# Revit family: UM375 Silla Lisa
name_source: partatom
category: Mobiliario
units: mm (PartAtom-declared; Revit-internal decimal feet)

## family parameters
Compartido = No
Corte con vacíos al cargar = No
Número OmniClass = 23.40.20.00
Punto de cálculo de habitación = No
Se basa en plano de trabajo = No
Siempre vertical = Sí
Título OmniClass = General Furniture and Specialties

## types (1)
- UM372SK Silla Kube Kurve
    Acabado Silla = Color gris granítico de aspecto rugoso.
    Accessibilidad = Sí
    Altura asiento = 450 mm  [stored 1.47638 ft]
    Altura total = 450 mm  [stored 1.47638 ft]
    Comentarios de tipo = Hormigón prefabricado color gris granítico de aspecto rugoso. Se puede colocar en elementos aislados o en grupos.
    Diámetro = 580 mm  [stored 1.90289 ft]
    Fabricante = BENITO
    Ficha tecnica = http://www.benito.com
    Instalación = Apoyado por su propio peso.
    Material Silla = Hormigón prefabricado.
    Modelo = Silla Kube Ficus
    Referencia = UM348S
    URL = http://www.benito.com
    URL Producto = http://www.benito.com

note: [stored X ft] marks values corroborated as IEEE doubles in the binary element streams (Revit-internal decimal feet)

## geometry (parser evidence)
native form markers: Blend x4
no freeform markers — native parametric forms only
